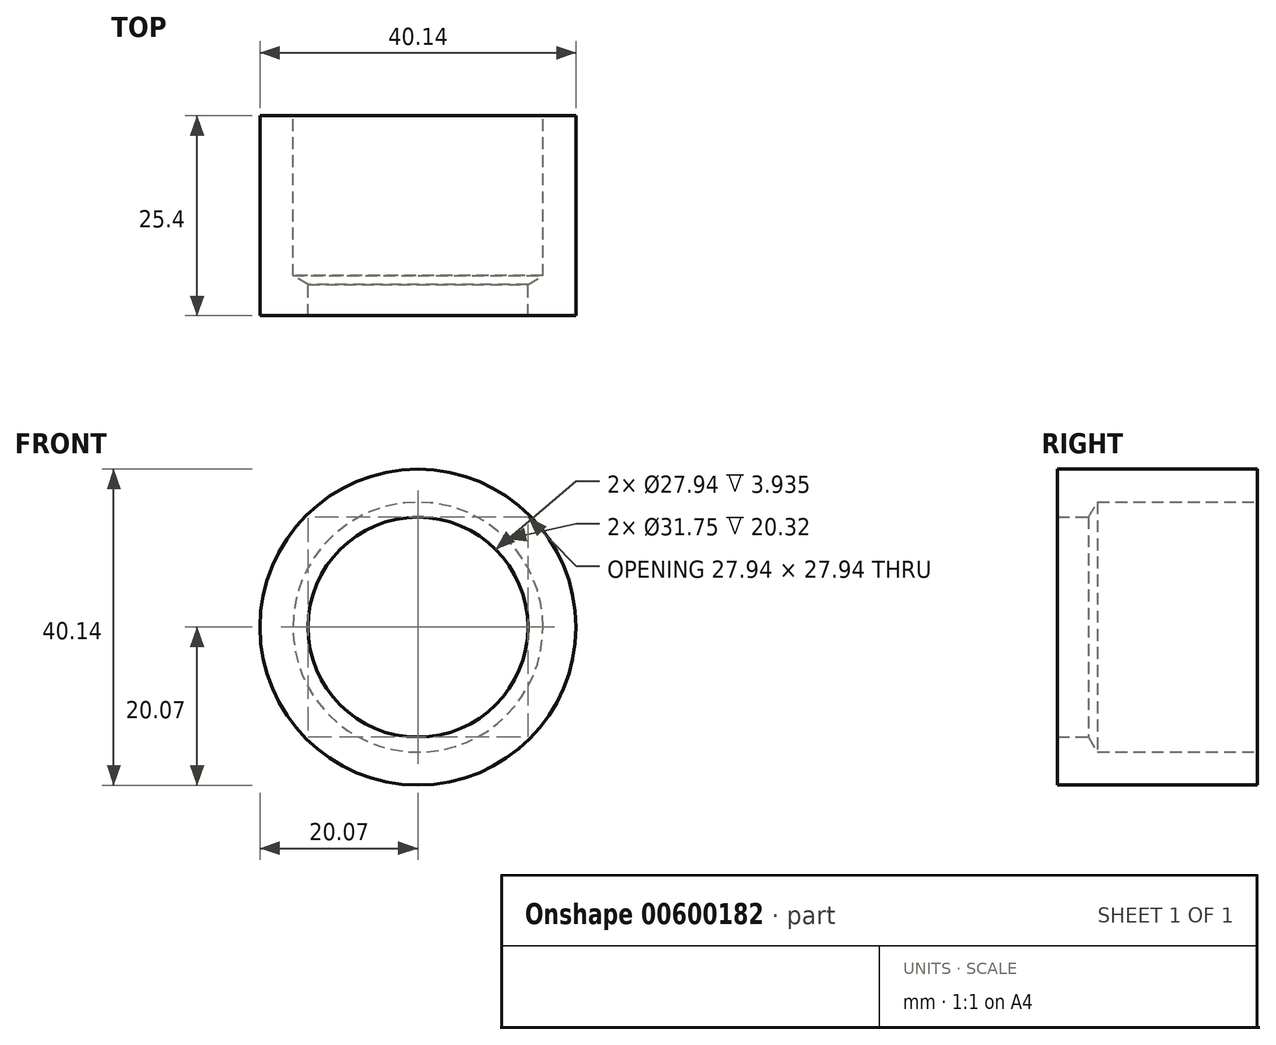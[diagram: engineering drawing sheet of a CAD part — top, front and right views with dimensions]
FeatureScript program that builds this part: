
annotation { "Feature Type Name" : "Feature", "Feature Type Description" : "" }
export const myFeature = defineFeature(function(context is Context, id is Id, definition is map)
    precondition{}
    {
        {
            var Q0;
            Q0=qCreatedBy(makeId("Front.planeOp"),FACE);
            var sketch = newSketch(context, id + "F0", { "sketchPlane" : qUnion([Q0])});
            skCircle(sketch, "E0", {"center": v(0, 0) * mm, "radius": 20.07 * mm});
            skCircle(sketch, "E1", {"center": v(0, 0) * mm, "radius": 13.97 * mm});
            skSolve(sketch);
        }
        {
            var Q0;
            Q0=makeQuery(id+"F0.imprint","IMPRINT",FACE,{"disambiguationData":[TD([[makeQuery(id+"F0.imprint","IMPRINT",EDGE,{"derivedFrom":sQuery(id+"F0.wireOp",EDGE,"E0")}),1.0]])]});
            extrude(context, id + "F1", {"entities" : qUnion([Q0]), "depth" : 25.4 * mm, "offsetDistance" : 25.4 * mm});
        }
        {
            var Q0;
            Q0=qCreatedBy(makeId("Front.planeOp"),FACE);
            var sketch = newSketch(context, id + "F2", { "sketchPlane" : qUnion([Q0])});
            skCircle(sketch, "E2", {"center": v(0, 0) * mm, "radius": 15.88 * mm});
            skSolve(sketch);
        }
        {
            var Q0;
            Q0=sQuery(id+"F2.wireOp",VERTEX,"E2.center");
            var Q1;
            Q1=makeQuery(id+"F1.opExtrude","SWEPT_BODY",BODY,{"disambiguationData":[OSD([sQuery(id+"F0.wireOp",EDGE,"E0"),sQuery(id+"F0.wireOp",EDGE,"E1")])]});
            hole(context, id + "F3", {"style" : HoleStyle.SIMPLE, "endStyle" : HoleEndStyle.BLIND, "oppositeDirection" : true, "holeDiameter" : 31.75 * mm, "majorDiameter" : 6.35 * mm, "holeDepth" : 20.32 * mm, "isTappedThrough" : true, "tappedDepth" : 12.7 * mm, "tapClearance" : 3, "startFromSketch" : true, "locations" : qUnion([Q0]), "scope" : qUnion([Q1])});
        }
    });
